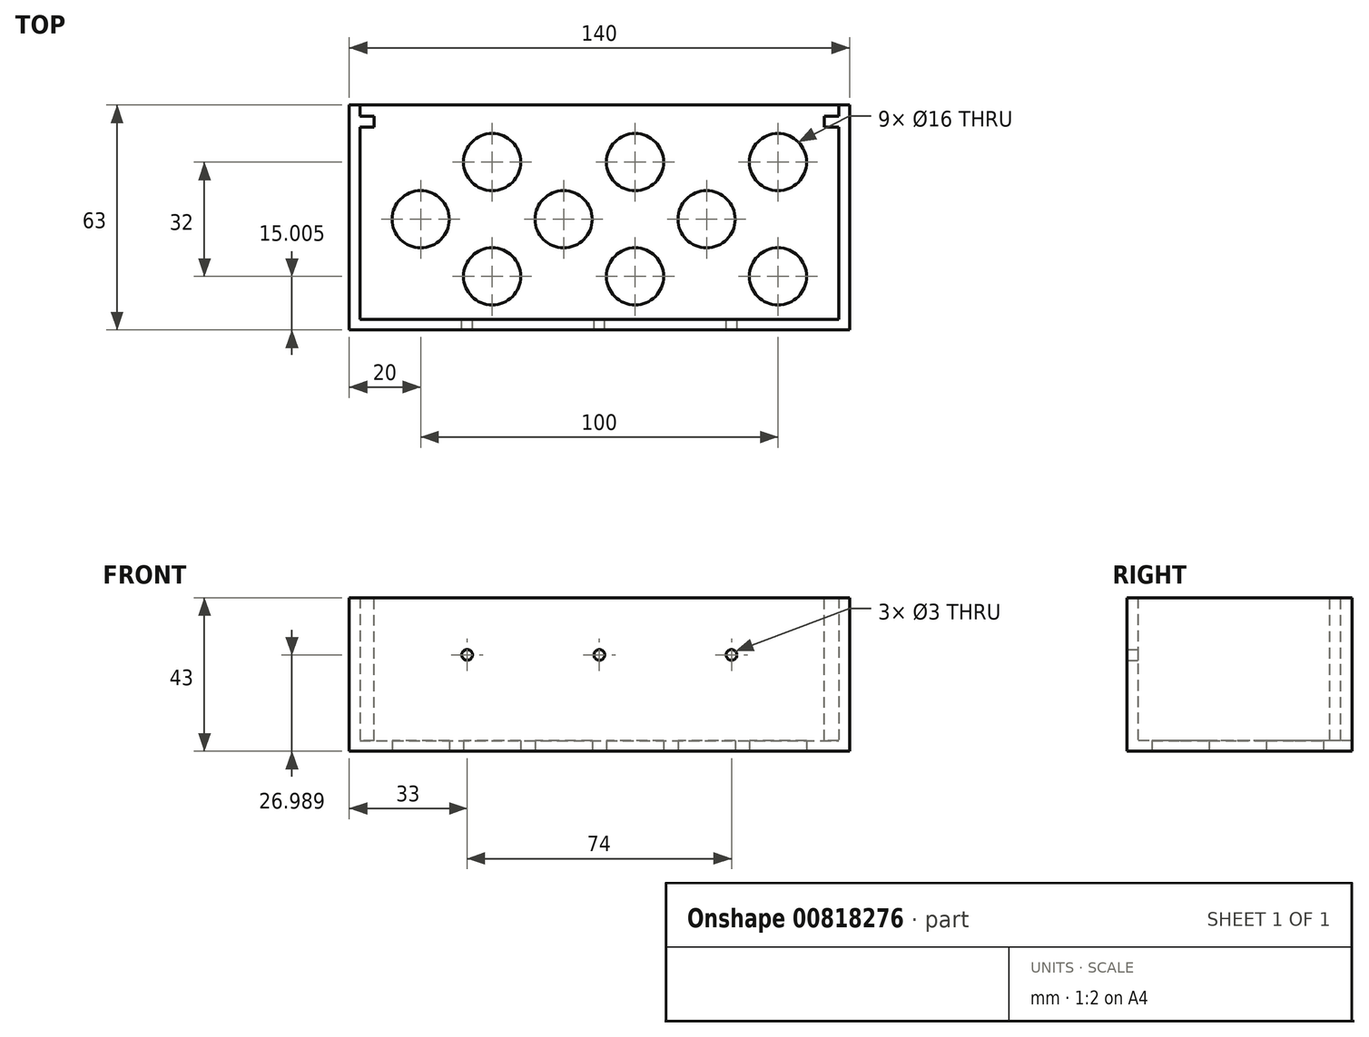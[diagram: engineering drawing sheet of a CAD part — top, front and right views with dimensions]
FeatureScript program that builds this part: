
annotation { "Feature Type Name" : "Feature", "Feature Type Description" : "" }
export const myFeature = defineFeature(function(context is Context, id is Id, definition is map)
    precondition{}
    {
        {
            var Q0;
            Q0=qCreatedBy(makeId("Top.planeOp"),FACE);
            var sketch = newSketch(context, id + "F0", { "sketchPlane" : qUnion([Q0])});
            skLineSegment(sketch, "E0.bottom", {"start": v(-80, 33.03) * mm, "end": v(60, 33.03) * mm});
            skLineSegment(sketch, "E0.top", {"start": v(-80, -32.97) * mm, "end": v(60, -32.97) * mm});
            skLineSegment(sketch, "E0.left", {"start": v(-80, 33.03) * mm, "end": v(-80, -32.97) * mm});
            skLineSegment(sketch, "E0.right", {"start": v(60, 33.03) * mm, "end": v(60, -32.97) * mm});
            skLineSegment(sketch, "E1.left", {"start": v(-80, -32.97) * mm, "end": v(-80, 0.03) * mm});
            skLineSegment(sketch, "E1.right", {"start": v(60, -9.97) * mm, "end": v(60, 0.03) * mm});
            skLineSegment(sketch, "E2.bottom", {"start": v(-80, -32.97) * mm, "end": v(-60, -32.97) * mm});
            skLineSegment(sketch, "E2.top", {"start": v(-80, 33.03) * mm, "end": v(-60, 33.03) * mm});
            skLineSegment(sketch, "E2.left", {"start": v(-80, -32.97) * mm, "end": v(-80, 33.03) * mm});
            skLineSegment(sketch, "E3.bottom", {"start": v(-60, -32.97) * mm, "end": v(-40, -32.97) * mm});
            skLineSegment(sketch, "E3.top", {"start": v(-60, 33.03) * mm, "end": v(-40, 33.03) * mm});
            skLineSegment(sketch, "E4.bottom", {"start": v(-40, -32.97) * mm, "end": v(-20, -32.97) * mm});
            skLineSegment(sketch, "E4.top", {"start": v(-40, 33.03) * mm, "end": v(-20, 33.03) * mm});
            skPoint(sketch, "E5.oppositeSnap0", {"position": v(-10, 33.03) * mm});
            skLineSegment(sketch, "E5.bottom", {"start": v(-20, -32.97) * mm, "end": v(0, -32.97) * mm});
            skLineSegment(sketch, "E5.top", {"start": v(-20, 33.03) * mm, "end": v(0, 33.03) * mm});
            skLineSegment(sketch, "E6.bottom", {"start": v(0, -32.97) * mm, "end": v(20, -32.97) * mm});
            skLineSegment(sketch, "E6.top", {"start": v(0, 33.03) * mm, "end": v(20, 33.03) * mm});
            skLineSegment(sketch, "E7.bottom", {"start": v(20, -32.97) * mm, "end": v(40, -32.97) * mm});
            skLineSegment(sketch, "E7.top", {"start": v(20, 33.03) * mm, "end": v(40, 33.03) * mm});
            skLineSegment(sketch, "E8.left", {"start": v(-80, -32.97) * mm, "end": v(-80, -2.97) * mm});
            skLineSegment(sketch, "E8.right", {"start": v(60, -24.97) * mm, "end": v(60, -4.97) * mm});
            skLineSegment(sketch, "E9.left", {"start": v(-80, 33.03) * mm, "end": v(-80, 18.03) * mm});
            skLineSegment(sketch, "E9.right", {"start": v(60, 33.03) * mm, "end": v(60, 18.03) * mm});
            skCircle(sketch, "E10", {"center": v(-60, 1.03) * mm, "radius": 8 * mm});
            skCircle(sketch, "E11", {"center": v(-40, 17.03) * mm, "radius": 8 * mm});
            skCircle(sketch, "E12", {"center": v(-20, 1.03) * mm, "radius": 8 * mm});
            skCircle(sketch, "E13", {"center": v(0, 17.03) * mm, "radius": 8 * mm});
            skCircle(sketch, "E14", {"center": v(20, 1.03) * mm, "radius": 8 * mm});
            skCircle(sketch, "E15", {"center": v(40, 17.03) * mm, "radius": 8 * mm});
            skLineSegment(sketch, "E16.left", {"start": v(-80, -32.97) * mm, "end": v(-80, -17.97) * mm});
            skLineSegment(sketch, "E16.right", {"start": v(60, -32.97) * mm, "end": v(60, -14.97) * mm});
            skCircle(sketch, "E17", {"center": v(-40, -14.97) * mm, "radius": 8 * mm});
            skCircle(sketch, "E18", {"center": v(0, -14.97) * mm, "radius": 8 * mm});
            skCircle(sketch, "E19", {"center": v(40, -14.97) * mm, "radius": 8 * mm});
            skLineSegment(sketch, "E20.top", {"start": v(-80, -29.97) * mm, "end": v(60, -29.97) * mm});
            skLineSegment(sketch, "E20.left", {"start": v(-80, -32.97) * mm, "end": v(-80, -29.97) * mm});
            skLineSegment(sketch, "E20.right", {"start": v(60, -32.97) * mm, "end": v(60, -29.97) * mm});
            skSolve(sketch);
        }
        {
            var Q0;
            Q0=makeQuery(id+"F0.imprint","IMPRINT",FACE,{"disambiguationData":[TD([[makeQuery(id+"F0.imprint","IMPRINT",EDGE,{"derivedFrom":sQuery(id+"F0.wireOp",EDGE,"E0.right")}),-1.0]])]});
            extrude(context, id + "F1", {"entities" : qUnion([Q0]), "depth" : 3 * mm, "offsetDistance" : 25 * mm});
        }
        {
            var Q0;
            Q0=makeQuery(id+"F1.opExtrude","CAP_FACE",FACE,{"disambiguationData":[OSD([sQuery(id+"F0.wireOp",EDGE,"E0.right"),sQuery(id+"F0.wireOp",EDGE,"E1.right"),sQuery(id+"F0.wireOp",EDGE,"E2.left"),sQuery(id+"F0.wireOp",EDGE,"E8.left"),sQuery(id+"F0.wireOp",EDGE,"E8.right"),sQuery(id+"F0.wireOp",EDGE,"E0.bottom"),sQuery(id+"F0.wireOp",EDGE,"E9.left"),sQuery(id+"F0.wireOp",EDGE,"E9.right"),sQuery(id+"F0.wireOp",EDGE,"E10"),sQuery(id+"F0.wireOp",EDGE,"E11"),sQuery(id+"F0.wireOp",EDGE,"E12"),sQuery(id+"F0.wireOp",EDGE,"E13"),sQuery(id+"F0.wireOp",EDGE,"E14"),sQuery(id+"F0.wireOp",EDGE,"E15"),sQuery(id+"F0.wireOp",EDGE,"E16.left"),sQuery(id+"F0.wireOp",EDGE,"E16.right"),sQuery(id+"F0.wireOp",EDGE,"E17"),sQuery(id+"F0.wireOp",EDGE,"E18"),sQuery(id+"F0.wireOp",EDGE,"E19"),sQuery(id+"F0.wireOp",EDGE,"E20.top")])],"isStart":false});
            var sketch = newSketch(context, id + "F2", { "sketchPlane" : qUnion([Q0])});
            skLineSegment(sketch, "E21.bottom", {"start": v(-80, -29.97) * mm, "end": v(60, -29.97) * mm});
            skLineSegment(sketch, "E21.top", {"start": v(-80, -26.97) * mm, "end": v(60, -26.97) * mm});
            skLineSegment(sketch, "E21.left", {"start": v(-80, -29.97) * mm, "end": v(-80, -26.97) * mm});
            skLineSegment(sketch, "E21.right", {"start": v(60, -29.97) * mm, "end": v(60, -26.97) * mm});
            skLineSegment(sketch, "E22.left", {"start": v(-80, 33.03) * mm, "end": v(-80, 30.03) * mm});
            skLineSegment(sketch, "E22.right", {"start": v(60, 33.03) * mm, "end": v(60, 30.03) * mm});
            skLineSegment(sketch, "E23.bottom", {"start": v(-80, 33.03) * mm, "end": v(-77, 33.03) * mm});
            skLineSegment(sketch, "E23.top", {"start": v(-80, -29.97) * mm, "end": v(-77, -29.97) * mm});
            skLineSegment(sketch, "E23.left", {"start": v(-80, 33.03) * mm, "end": v(-80, -29.97) * mm});
            skLineSegment(sketch, "E23.right", {"start": v(-77, 33.03) * mm, "end": v(-77, -29.97) * mm});
            skLineSegment(sketch, "E24.bottom", {"start": v(60, 33.03) * mm, "end": v(57, 33.03) * mm});
            skLineSegment(sketch, "E24.top", {"start": v(60, -29.97) * mm, "end": v(57, -29.97) * mm});
            skLineSegment(sketch, "E24.left", {"start": v(60, 33.03) * mm, "end": v(60, -29.97) * mm});
            skLineSegment(sketch, "E24.right", {"start": v(57, 33.03) * mm, "end": v(57, -29.97) * mm});
            skSolve(sketch);
        }
        {
            var Q0;
            Q0 = qSketchRegion(id + "F2", true);
            extrude(context, id + "F3", {"entities" : qUnion([Q0]), "operationType" : NewBodyOperationType.ADD, "depth" : 40 * mm, "offsetDistance" : 25 * mm});
        }
        {
            var Q0;
            Q0=makeQuery(id+"F3.opExtrude","SWEPT_FACE",FACE,{"disambiguationData":[OSD([sQuery(id+"F2.wireOp",EDGE,"E23.right")])]});
            var sketch = newSketch(context, id + "F4", { "sketchPlane" : qUnion([Q0])});
            skLineSegment(sketch, "E25.bottom", {"start": v(33.03, 43) * mm, "end": v(29.83, 43) * mm});
            skLineSegment(sketch, "E25.top", {"start": v(33.03, 3) * mm, "end": v(29.83, 3) * mm});
            skLineSegment(sketch, "E25.left", {"start": v(33.03, 43) * mm, "end": v(33.03, 3) * mm});
            skLineSegment(sketch, "E25.right", {"start": v(29.83, 43) * mm, "end": v(29.83, 3) * mm});
            skLineSegment(sketch, "E26.bottom", {"start": v(29.83, 43) * mm, "end": v(26.83, 43) * mm});
            skLineSegment(sketch, "E26.top", {"start": v(29.83, 3) * mm, "end": v(26.83, 3) * mm});
            skLineSegment(sketch, "E26.right", {"start": v(26.83, 43) * mm, "end": v(26.83, 3) * mm});
            skSolve(sketch);
        }
        {
            var Q0;
            Q0=makeQuery(id+"F4.imprint","IMPRINT",FACE,{"disambiguationData":[TD([[makeQuery(id+"F4.imprint","IMPRINT",EDGE,{"derivedFrom":sQuery(id+"F4.wireOp",EDGE,"E26.bottom")}),1.0]])]});
            extrude(context, id + "F5", {"entities" : qUnion([Q0]), "operationType" : NewBodyOperationType.ADD, "depth" : 134 * mm, "offsetDistance" : 25 * mm});
        }
        {
            var Q0;
            Q0=makeQuery(id+"F5.boolean.opBoolean","MERGE",FACE,{"derivedFrom":[makeQuery(id+"F3.opExtrude","CAP_FACE",FACE,{"disambiguationData":[OSD([sQuery(id+"F2.wireOp",EDGE,"E21.bottom"),sQuery(id+"F2.wireOp",EDGE,"E21.top"),sQuery(id+"F2.wireOp",EDGE,"E23.bottom"),sQuery(id+"F2.wireOp",EDGE,"E23.top"),sQuery(id+"F2.wireOp",EDGE,"E23.left"),sQuery(id+"F2.wireOp",EDGE,"E23.right"),sQuery(id+"F2.wireOp",EDGE,"E24.bottom"),sQuery(id+"F2.wireOp",EDGE,"E24.top"),sQuery(id+"F2.wireOp",EDGE,"E24.left"),sQuery(id+"F2.wireOp",EDGE,"E24.right")])],"isStart":false}),makeQuery(id+"F5.opExtrude","SWEPT_FACE",FACE,{"disambiguationData":[OSD([sQuery(id+"F4.wireOp",EDGE,"E26.bottom")])]})]});
            var sketch = newSketch(context, id + "F6", { "sketchPlane" : qUnion([Q0])});
            skLineSegment(sketch, "E27.bottom", {"start": v(-73, 29.83) * mm, "end": v(53, 29.83) * mm});
            skLineSegment(sketch, "E27.top", {"start": v(-73, 26.83) * mm, "end": v(53, 26.83) * mm});
            skLineSegment(sketch, "E27.left", {"start": v(-73, 29.83) * mm, "end": v(-73, 26.83) * mm});
            skLineSegment(sketch, "E27.right", {"start": v(53, 29.83) * mm, "end": v(53, 26.83) * mm});
            skSolve(sketch);
        }
        {
            var Q0;
            Q0 = qSketchRegion(id + "F6", true);
            extrude(context, id + "F7", {"entities" : qUnion([Q0]), "operationType" : NewBodyOperationType.REMOVE, "oppositeDirection" : true, "depth" : 40 * mm, "offsetDistance" : 25 * mm});
        }
        {
            var Q0;
            Q0=makeQuery(id+"F3.opExtrude","SWEPT_FACE",FACE,{"disambiguationData":[OSD([sQuery(id+"F2.wireOp",EDGE,"E21.top")])]});
            var sketch = newSketch(context, id + "F8", { "sketchPlane" : qUnion([Q0])});
            skLineSegment(sketch, "E28.bottom", {"start": v(77, 43) * mm, "end": v(-57, 43) * mm});
            skLineSegment(sketch, "E28.left", {"start": v(77, 43) * mm, "end": v(77, 26.99) * mm});
            skLineSegment(sketch, "E28.right", {"start": v(-57, 43) * mm, "end": v(-57, 26.99) * mm});
            skCircle(sketch, "E29", {"center": v(47, 26.99) * mm, "radius": 1.5 * mm});
            skCircle(sketch, "E30", {"center": v(-27, 26.99) * mm, "radius": 1.5 * mm});
            skCircle(sketch, "E31", {"center": v(10, 26.99) * mm, "radius": 1.5 * mm});
            skSolve(sketch);
        }
        {
            var Q0;
            Q0=makeQuery(id+"F8.imprint","IMPRINT",FACE,{"disambiguationData":[TD([[makeQuery(id+"F8.imprint","IMPRINT",EDGE,{"derivedFrom":sQuery(id+"F8.wireOp",EDGE,"E29")}),1.0]])]});
            var Q1;
            Q1=makeQuery(id+"F8.imprint","IMPRINT",FACE,{"disambiguationData":[TD([[makeQuery(id+"F8.imprint","IMPRINT",EDGE,{"derivedFrom":sQuery(id+"F8.wireOp",EDGE,"E30")}),1.0]])]});
            var Q2;
            Q2=makeQuery(id+"F8.imprint","IMPRINT",FACE,{"disambiguationData":[TD([[makeQuery(id+"F8.imprint","IMPRINT",EDGE,{"derivedFrom":sQuery(id+"F8.wireOp",EDGE,"E31")}),1.0]])]});
            extrude(context, id + "F9", {"entities" : qUnion([Q0, Q1, Q2]), "operationType" : NewBodyOperationType.REMOVE, "oppositeDirection" : true, "depth" : 3 * mm, "offsetDistance" : 25 * mm});
        }
    });
